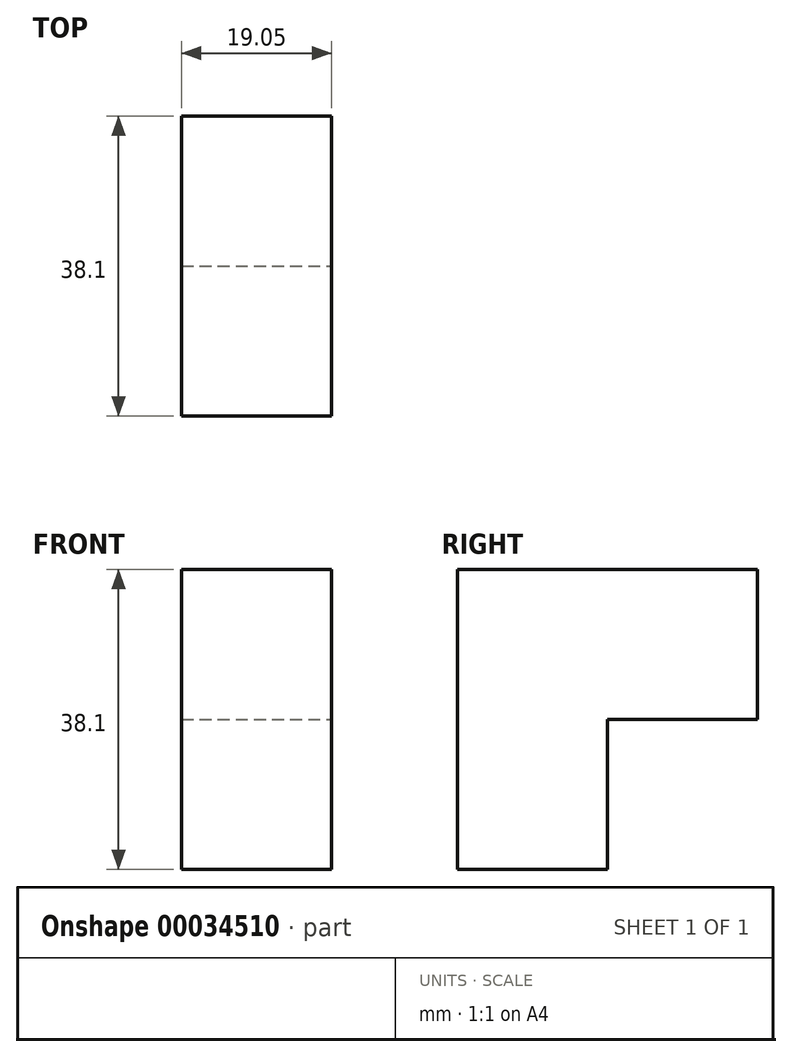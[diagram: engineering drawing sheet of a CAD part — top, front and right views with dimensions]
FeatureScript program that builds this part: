
annotation { "Feature Type Name" : "Feature", "Feature Type Description" : "" }
export const myFeature = defineFeature(function(context is Context, id is Id, definition is map)
    precondition{}
    {
        {
            var Q0;
            Q0=qCreatedBy(makeId("Right.planeOp"),FACE);
            var sketch = newSketch(context, id + "F0", { "sketchPlane" : qUnion([Q0])});
            skLineSegment(sketch, "E0.bottom", {"start": v(0, 0) * mm, "end": v(38.1, 0) * mm});
            skLineSegment(sketch, "E0.top", {"start": v(0, 38.1) * mm, "end": v(38.1, 38.1) * mm});
            skLineSegment(sketch, "E0.left", {"start": v(0, 0) * mm, "end": v(0, 38.1) * mm});
            skLineSegment(sketch, "E0.right", {"start": v(38.1, 0) * mm, "end": v(38.1, 38.1) * mm});
            skSolve(sketch);
        }
        {
            var Q0;
            Q0 = qSketchRegion(id + "F0", true);
            extrude(context, id + "F1", {"entities" : qUnion([Q0]), "depth" : 19.05 * mm});
        }
        {
            var Q0;
            Q0=makeQuery(id+"F1.opExtrude","CAP_FACE",FACE,{"disambiguationData":[OSD([sQuery(id+"F0.wireOp",EDGE,"E0.bottom"),sQuery(id+"F0.wireOp",EDGE,"E0.top"),sQuery(id+"F0.wireOp",EDGE,"E0.left"),sQuery(id+"F0.wireOp",EDGE,"E0.right")])],"isStart":false});
            var sketch = newSketch(context, id + "F2", { "sketchPlane" : qUnion([Q0])});
            skLineSegment(sketch, "E1.bottom", {"start": v(38.1, 0) * mm, "end": v(19.05, 0) * mm});
            skLineSegment(sketch, "E1.top", {"start": v(38.1, 19.05) * mm, "end": v(19.05, 19.05) * mm});
            skLineSegment(sketch, "E1.left", {"start": v(38.1, 0) * mm, "end": v(38.1, 19.05) * mm});
            skLineSegment(sketch, "E1.right", {"start": v(19.05, 0) * mm, "end": v(19.05, 19.05) * mm});
            skSolve(sketch);
        }
        {
            var Q0;
            Q0 = qSketchRegion(id + "F2", true);
            extrude(context, id + "F3", {"entities" : qUnion([Q0]), "operationType" : NewBodyOperationType.REMOVE, "oppositeDirection" : true, "depth" : 19.05 * mm});
        }
    });
